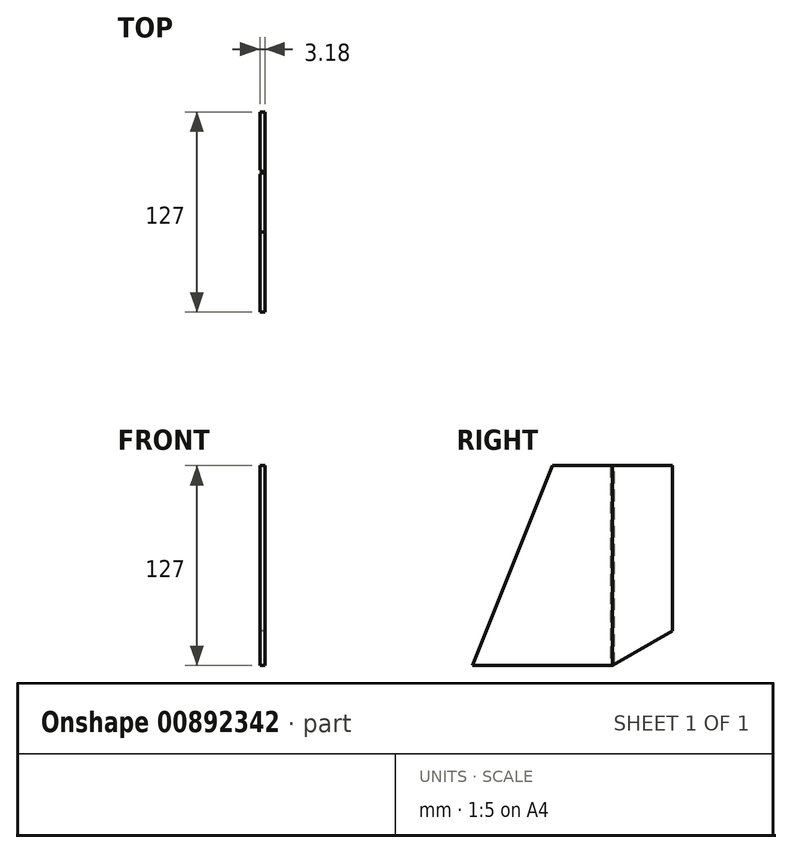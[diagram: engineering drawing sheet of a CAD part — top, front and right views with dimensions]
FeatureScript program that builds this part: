
annotation { "Feature Type Name" : "Feature", "Feature Type Description" : "" }
export const myFeature = defineFeature(function(context is Context, id is Id, definition is map)
    precondition{}
    {
        {
            var Q0;
            Q0=qCreatedBy(makeId("Right.planeOp"),FACE);
            var sketch = newSketch(context, id + "F0", { "sketchPlane" : qUnion([Q0])});
            skLineSegment(sketch, "E0", {"start": v(0, 0) * mm, "end": v(-88.9, 0) * mm});
            skLineSegment(sketch, "E1", {"start": v(0, 0) * mm, "end": v(0, 127) * mm});
            skLineSegment(sketch, "E2", {"start": v(-88.9, 0) * mm, "end": v(-38.1, 127) * mm});
            skLineSegment(sketch, "E3", {"start": v(-38.1, 127) * mm, "end": v(0, 127) * mm});
            skLineSegment(sketch, "E4", {"start": v(0, 127) * mm, "end": v(38.1, 127) * mm});
            skLineSegment(sketch, "E5", {"start": v(38.1, 127) * mm, "end": v(38.1, 21.9) * mm});
            skLineSegment(sketch, "E6", {"start": v(0, 0) * mm, "end": v(38.1, 21.9) * mm});
            skPoint(sketch, "E7.end.orphan", {"position": v(38.1, 0) * mm});
            skSolve(sketch);
        }
        {
            var Q0;
            Q0=makeQuery(id+"F0.imprint","IMPRINT",FACE,{"disambiguationData":[TD([[makeQuery(id+"F0.imprint","IMPRINT",EDGE,{"derivedFrom":sQuery(id+"F0.wireOp",EDGE,"E0")}),-1.0]])]});
            extrude(context, id + "F1", {"entities" : qUnion([Q0]), "endBound" : BoundingType.SYMMETRIC, "depth" : 3.17 * mm, "offsetDistance" : 25.4 * mm});
        }
        {
            var Q0;
            Q0=makeQuery(id+"F0.imprint","IMPRINT",FACE,{"disambiguationData":[TD([[makeQuery(id+"F0.imprint","IMPRINT",EDGE,{"derivedFrom":sQuery(id+"F0.wireOp",EDGE,"E1")}),-1.0]])]});
            extrude(context, id + "F2", {"entities" : qUnion([Q0]), "endBound" : BoundingType.SYMMETRIC, "depth" : 3.17 * mm, "offsetDistance" : 25.4 * mm});
        }
        {
            var Q0;
            Q0=makeQuery(id+"F1.opExtrude","CAP_EDGE",EDGE,{"disambiguationData":[OSD([sQuery(id+"F0.wireOp",EDGE,"E1")])],"isStart":true});
            chamfer(context, id + "F3", {"entities" : qUnion([Q0]), "chamferType" : ChamferType.OFFSET_ANGLE, "width" : 3.3 * mm, "oppositeDirection" : false, "angle" : 22.5 * degree, "tangentPropagation" : true});
        }
        {
            var Q0;
            Q0=makeQuery(id+"F2.opExtrude","CAP_EDGE",EDGE,{"disambiguationData":[OSD([sQuery(id+"F0.wireOp",EDGE,"E1")])],"isStart":true});
            chamfer(context, id + "F4", {"entities" : qUnion([Q0]), "chamferType" : ChamferType.OFFSET_ANGLE, "width" : 3.05 * mm, "oppositeDirection" : true, "angle" : 22.5 * degree, "tangentPropagation" : true});
        }
    });
